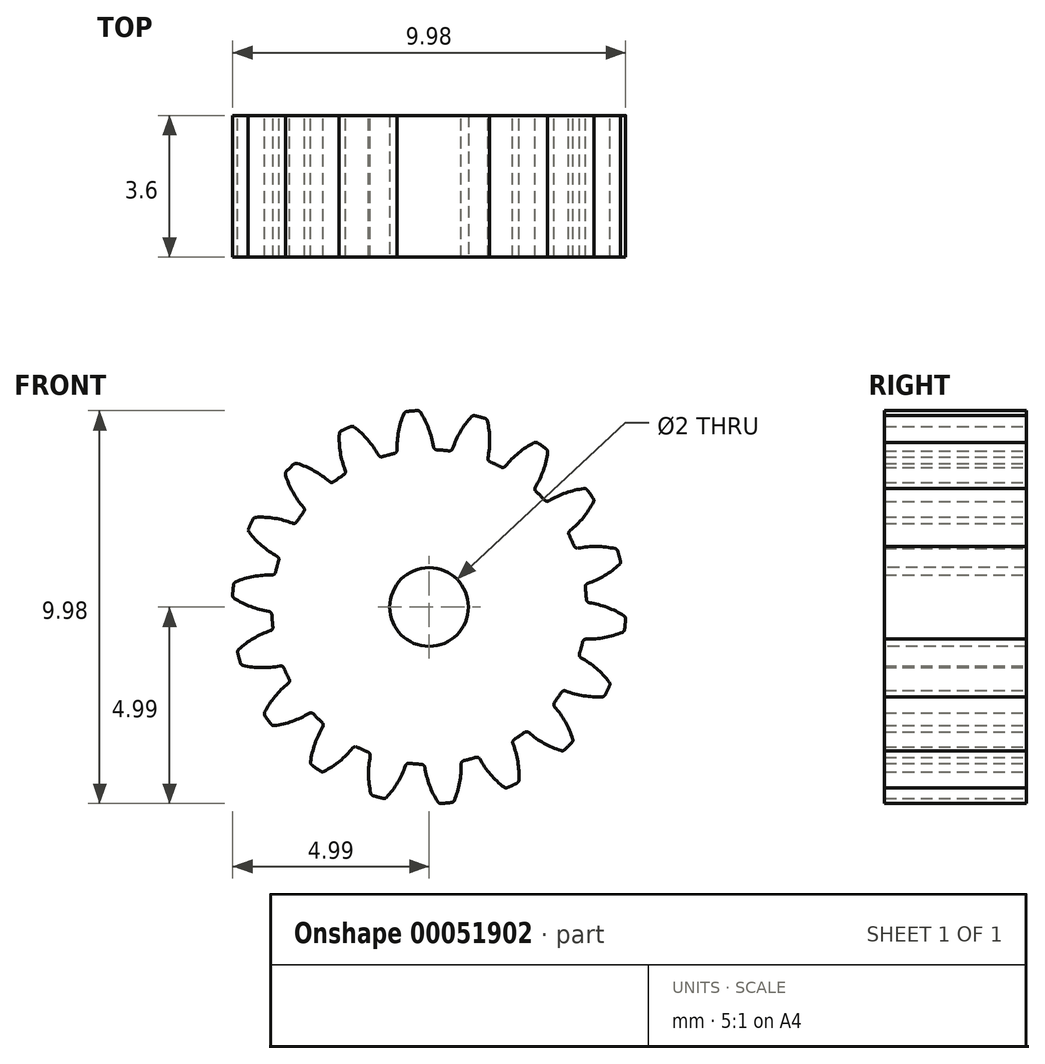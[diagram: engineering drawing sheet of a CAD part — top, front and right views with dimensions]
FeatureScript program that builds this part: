
annotation { "Feature Type Name" : "Feature", "Feature Type Description" : "" }
export const myFeature = defineFeature(function(context is Context, id is Id, definition is map)
    precondition{}
    {
        {
            var Q0;
            Q0=qCreatedBy(makeId("Front.planeOp"),FACE);
            var sketch = newSketch(context, id + "F0", { "sketchPlane" : qUnion([Q0])});
            skCircle(sketch, "E0", {"center": v(0, 0) * mm, "radius": 5 * mm, "construction": true});
            skCircle(sketch, "E1", {"center": v(0, 0) * mm, "radius": 4.5 * mm, "construction": true});
            skCircle(sketch, "E2", {"center": v(0, 0) * mm, "radius": 4 * mm, "construction": true});
            skLineSegment(sketch, "E3", {"start": v(0, 0) * mm, "end": v(0, 8.94) * mm, "construction": true});
            skLineSegment(sketch, "E4", {"start": v(0, 0) * mm, "end": v(-0.76, 8.67) * mm, "construction": true});
            skLineSegment(sketch, "E5", {"start": v(0, 4.5) * mm, "end": v(-8.84, 4.5) * mm, "construction": true});
            skLineSegment(sketch, "E6", {"start": v(0, 4.5) * mm, "end": v(-8.62, 1.36) * mm, "construction": true});
            skCircle(sketch, "E7", {"center": v(0, 4.5) * mm, "radius": 2.25 * mm, "construction": true});
            skCircle(sketch, "E8", {"center": v(-2.11, 3.73) * mm, "radius": 2.25 * mm, "construction": true});
            skArc(sketch, "E9", {"start": v(-0.25, 5) * mm, "mid": v(0, 4.52) * mm, "end": v(0.12, 4) * mm, "construction": true});
            skArc(sketch, "E10", {"start": v(-0.22, 4.95) * mm, "mid": v(-0.01, 4.53) * mm, "end": v(0.1, 4.07) * mm});
            skArc(sketch, "E11.MirrorCS", {"start": v(-0.64, 4.91) * mm, "mid": v(-0.78, 4.46) * mm, "end": v(-0.82, 4) * mm});
            skArc(sketch, "E12", {"start": v(-0.57, 4.97) * mm, "mid": v(-0.44, 4.98) * mm, "end": v(-0.3, 5) * mm});
            skArc(sketch, "E13", {"start": v(-0.89, 3.9) * mm, "mid": v(0.35, -3.98) * mm, "end": v(0.2, 4) * mm});
            skPoint(sketch, "E14.visualSharp", {"position": v(-0.81, 3.92) * mm});
            skArc(sketch, "E14.filletArc", {"start": v(-0.89, 3.9) * mm, "mid": v(-0.83, 3.93) * mm, "end": v(-0.82, 4) * mm});
            skPoint(sketch, "E15.visualSharp", {"position": v(-0.62, 4.96) * mm});
            skArc(sketch, "E15.filletArc", {"start": v(-0.57, 4.97) * mm, "mid": v(-0.61, 4.95) * mm, "end": v(-0.64, 4.91) * mm});
            skPoint(sketch, "E16.visualSharp", {"position": v(0.12, 4) * mm});
            skArc(sketch, "E16.filletArc", {"start": v(0.1, 4.07) * mm, "mid": v(0.14, 4.02) * mm, "end": v(0.2, 4) * mm});
            skPoint(sketch, "E17.visualSharp", {"position": v(-0.25, 5) * mm});
            skArc(sketch, "E17.filletArc", {"start": v(-0.22, 4.95) * mm, "mid": v(-0.26, 4.98) * mm, "end": v(-0.3, 5) * mm});
            skArc(sketch, "E18.1.0", {"start": v(-2.17, 3.36) * mm, "mid": v(-2.13, 3.41) * mm, "end": v(-2.13, 3.47) * mm});
            skArc(sketch, "E18.1.1", {"start": v(-2.28, 4.4) * mm, "mid": v(-2.26, 3.93) * mm, "end": v(-2.13, 3.47) * mm});
            skArc(sketch, "E18.1.2", {"start": v(-2.23, 4.47) * mm, "mid": v(-2.27, 4.44) * mm, "end": v(-2.28, 4.4) * mm});
            skArc(sketch, "E18.1.3", {"start": v(-2.23, 4.47) * mm, "mid": v(-2.11, 4.53) * mm, "end": v(-2, 4.59) * mm});
            skArc(sketch, "E18.1.4", {"start": v(-1.9, 4.57) * mm, "mid": v(-1.95, 4.6) * mm, "end": v(-2, 4.59) * mm});
            skArc(sketch, "E18.1.5", {"start": v(-1.9, 4.57) * mm, "mid": v(-1.56, 4.25) * mm, "end": v(-1.29, 3.86) * mm});
            skArc(sketch, "E18.1.6", {"start": v(-1.29, 3.86) * mm, "mid": v(-1.24, 3.82) * mm, "end": v(-1.18, 3.82) * mm});
            skArc(sketch, "E18.2.0", {"start": v(-3.19, 2.42) * mm, "mid": v(-3.17, 2.48) * mm, "end": v(-3.19, 2.53) * mm});
            skArc(sketch, "E18.2.1", {"start": v(-3.65, 3.35) * mm, "mid": v(-3.46, 2.92) * mm, "end": v(-3.19, 2.53) * mm});
            skArc(sketch, "E18.2.2", {"start": v(-3.63, 3.44) * mm, "mid": v(-3.65, 3.4) * mm, "end": v(-3.65, 3.35) * mm});
            skArc(sketch, "E18.2.3", {"start": v(-3.63, 3.44) * mm, "mid": v(-3.54, 3.54) * mm, "end": v(-3.44, 3.63) * mm});
            skArc(sketch, "E18.2.4", {"start": v(-3.35, 3.65) * mm, "mid": v(-3.4, 3.65) * mm, "end": v(-3.44, 3.63) * mm});
            skArc(sketch, "E18.2.5", {"start": v(-3.35, 3.65) * mm, "mid": v(-2.92, 3.46) * mm, "end": v(-2.53, 3.19) * mm});
            skArc(sketch, "E18.2.6", {"start": v(-2.53, 3.19) * mm, "mid": v(-2.48, 3.17) * mm, "end": v(-2.42, 3.19) * mm});
            skArc(sketch, "E18.3.0", {"start": v(-3.82, 1.18) * mm, "mid": v(-3.82, 1.24) * mm, "end": v(-3.86, 1.29) * mm});
            skArc(sketch, "E18.3.1", {"start": v(-4.57, 1.9) * mm, "mid": v(-4.25, 1.56) * mm, "end": v(-3.86, 1.29) * mm});
            skArc(sketch, "E18.3.2", {"start": v(-4.59, 2) * mm, "mid": v(-4.6, 1.95) * mm, "end": v(-4.57, 1.9) * mm});
            skArc(sketch, "E18.3.3", {"start": v(-4.59, 2) * mm, "mid": v(-4.53, 2.11) * mm, "end": v(-4.47, 2.23) * mm});
            skArc(sketch, "E18.3.4", {"start": v(-4.4, 2.28) * mm, "mid": v(-4.44, 2.27) * mm, "end": v(-4.47, 2.23) * mm});
            skArc(sketch, "E18.3.5", {"start": v(-4.4, 2.28) * mm, "mid": v(-3.93, 2.26) * mm, "end": v(-3.47, 2.13) * mm});
            skArc(sketch, "E18.3.6", {"start": v(-3.47, 2.13) * mm, "mid": v(-3.41, 2.13) * mm, "end": v(-3.36, 2.17) * mm});
            skArc(sketch, "E18.4.0", {"start": v(-4, -0.2) * mm, "mid": v(-4.02, -0.14) * mm, "end": v(-4.07, -0.1) * mm});
            skArc(sketch, "E18.4.1", {"start": v(-4.95, 0.22) * mm, "mid": v(-4.53, 0.01) * mm, "end": v(-4.07, -0.1) * mm});
            skArc(sketch, "E18.4.2", {"start": v(-5, 0.3) * mm, "mid": v(-4.98, 0.26) * mm, "end": v(-4.95, 0.22) * mm});
            skArc(sketch, "E18.4.3", {"start": v(-5, 0.3) * mm, "mid": v(-4.98, 0.44) * mm, "end": v(-4.97, 0.57) * mm});
            skArc(sketch, "E18.4.4", {"start": v(-4.91, 0.64) * mm, "mid": v(-4.95, 0.61) * mm, "end": v(-4.97, 0.57) * mm});
            skArc(sketch, "E18.4.5", {"start": v(-4.91, 0.64) * mm, "mid": v(-4.46, 0.78) * mm, "end": v(-4, 0.82) * mm});
            skArc(sketch, "E18.4.6", {"start": v(-4, 0.82) * mm, "mid": v(-3.93, 0.83) * mm, "end": v(-3.9, 0.89) * mm});
            skArc(sketch, "E18.5.0", {"start": v(-3.69, -1.55) * mm, "mid": v(-3.73, -1.5) * mm, "end": v(-3.79, -1.5) * mm});
            skArc(sketch, "E18.5.1", {"start": v(-4.73, -1.48) * mm, "mid": v(-4.26, -1.54) * mm, "end": v(-3.79, -1.5) * mm});
            skArc(sketch, "E18.5.2", {"start": v(-4.8, -1.42) * mm, "mid": v(-4.77, -1.46) * mm, "end": v(-4.73, -1.48) * mm});
            skArc(sketch, "E18.5.3", {"start": v(-4.8, -1.42) * mm, "mid": v(-4.83, -1.3) * mm, "end": v(-4.86, -1.17) * mm});
            skArc(sketch, "E18.5.4", {"start": v(-4.84, -1.08) * mm, "mid": v(-4.86, -1.12) * mm, "end": v(-4.86, -1.17) * mm});
            skArc(sketch, "E18.5.5", {"start": v(-4.84, -1.08) * mm, "mid": v(-4.46, -0.8) * mm, "end": v(-4.03, -0.6) * mm});
            skArc(sketch, "E18.5.6", {"start": v(-4.03, -0.6) * mm, "mid": v(-3.98, -0.56) * mm, "end": v(-3.97, -0.5) * mm});
            skArc(sketch, "E18.6.0", {"start": v(-2.94, -2.72) * mm, "mid": v(-2.99, -2.69) * mm, "end": v(-3.05, -2.7) * mm});
            skArc(sketch, "E18.6.1", {"start": v(-3.94, -3.01) * mm, "mid": v(-3.48, -2.9) * mm, "end": v(-3.05, -2.7) * mm});
            skArc(sketch, "E18.6.2", {"start": v(-4.02, -2.97) * mm, "mid": v(-3.98, -3) * mm, "end": v(-3.94, -3.01) * mm});
            skArc(sketch, "E18.6.3", {"start": v(-4.02, -2.97) * mm, "mid": v(-4.1, -2.87) * mm, "end": v(-4.17, -2.76) * mm});
            skArc(sketch, "E18.6.4", {"start": v(-4.17, -2.67) * mm, "mid": v(-4.18, -2.71) * mm, "end": v(-4.17, -2.76) * mm});
            skArc(sketch, "E18.6.5", {"start": v(-4.17, -2.67) * mm, "mid": v(-3.92, -2.27) * mm, "end": v(-3.58, -1.94) * mm});
            skArc(sketch, "E18.6.6", {"start": v(-3.58, -1.94) * mm, "mid": v(-3.55, -1.89) * mm, "end": v(-3.56, -1.83) * mm});
            skArc(sketch, "E18.7.0", {"start": v(-1.83, -3.56) * mm, "mid": v(-1.89, -3.55) * mm, "end": v(-1.94, -3.58) * mm});
            skArc(sketch, "E18.7.1", {"start": v(-2.67, -4.17) * mm, "mid": v(-2.27, -3.92) * mm, "end": v(-1.94, -3.58) * mm});
            skArc(sketch, "E18.7.2", {"start": v(-2.76, -4.17) * mm, "mid": v(-2.71, -4.18) * mm, "end": v(-2.67, -4.17) * mm});
            skArc(sketch, "E18.7.3", {"start": v(-2.76, -4.17) * mm, "mid": v(-2.87, -4.1) * mm, "end": v(-2.97, -4.02) * mm});
            skArc(sketch, "E18.7.4", {"start": v(-3.01, -3.94) * mm, "mid": v(-3, -3.98) * mm, "end": v(-2.97, -4.02) * mm});
            skArc(sketch, "E18.7.5", {"start": v(-3.01, -3.94) * mm, "mid": v(-2.9, -3.48) * mm, "end": v(-2.7, -3.05) * mm});
            skArc(sketch, "E18.7.6", {"start": v(-2.7, -3.05) * mm, "mid": v(-2.69, -2.99) * mm, "end": v(-2.72, -2.94) * mm});
            skArc(sketch, "E18.8.0", {"start": v(-0.5, -3.97) * mm, "mid": v(-0.56, -3.98) * mm, "end": v(-0.6, -4.03) * mm});
            skArc(sketch, "E18.8.1", {"start": v(-1.08, -4.84) * mm, "mid": v(-0.8, -4.46) * mm, "end": v(-0.6, -4.03) * mm});
            skArc(sketch, "E18.8.2", {"start": v(-1.17, -4.86) * mm, "mid": v(-1.12, -4.86) * mm, "end": v(-1.08, -4.84) * mm});
            skArc(sketch, "E18.8.3", {"start": v(-1.17, -4.86) * mm, "mid": v(-1.3, -4.83) * mm, "end": v(-1.42, -4.8) * mm});
            skArc(sketch, "E18.8.4", {"start": v(-1.48, -4.73) * mm, "mid": v(-1.46, -4.77) * mm, "end": v(-1.42, -4.8) * mm});
            skArc(sketch, "E18.8.5", {"start": v(-1.48, -4.73) * mm, "mid": v(-1.54, -4.26) * mm, "end": v(-1.5, -3.79) * mm});
            skArc(sketch, "E18.8.6", {"start": v(-1.5, -3.79) * mm, "mid": v(-1.5, -3.73) * mm, "end": v(-1.55, -3.69) * mm});
            skArc(sketch, "E18.9.0", {"start": v(0.89, -3.9) * mm, "mid": v(0.83, -3.93) * mm, "end": v(0.82, -4) * mm});
            skArc(sketch, "E18.9.1", {"start": v(0.64, -4.91) * mm, "mid": v(0.78, -4.46) * mm, "end": v(0.82, -4) * mm});
            skArc(sketch, "E18.9.2", {"start": v(0.57, -4.97) * mm, "mid": v(0.61, -4.95) * mm, "end": v(0.64, -4.91) * mm});
            skArc(sketch, "E18.9.3", {"start": v(0.57, -4.97) * mm, "mid": v(0.44, -4.98) * mm, "end": v(0.3, -5) * mm});
            skArc(sketch, "E18.9.4", {"start": v(0.22, -4.95) * mm, "mid": v(0.26, -4.98) * mm, "end": v(0.3, -5) * mm});
            skArc(sketch, "E18.9.5", {"start": v(0.22, -4.95) * mm, "mid": v(0.01, -4.53) * mm, "end": v(-0.1, -4.07) * mm});
            skArc(sketch, "E18.9.6", {"start": v(-0.1, -4.07) * mm, "mid": v(-0.14, -4.02) * mm, "end": v(-0.2, -4) * mm});
            skArc(sketch, "E18.10.0", {"start": v(2.17, -3.36) * mm, "mid": v(2.13, -3.41) * mm, "end": v(2.13, -3.47) * mm});
            skArc(sketch, "E18.10.1", {"start": v(2.28, -4.4) * mm, "mid": v(2.26, -3.93) * mm, "end": v(2.13, -3.47) * mm});
            skArc(sketch, "E18.10.2", {"start": v(2.23, -4.47) * mm, "mid": v(2.27, -4.44) * mm, "end": v(2.28, -4.4) * mm});
            skArc(sketch, "E18.10.3", {"start": v(2.23, -4.47) * mm, "mid": v(2.11, -4.53) * mm, "end": v(2, -4.59) * mm});
            skArc(sketch, "E18.10.4", {"start": v(1.9, -4.57) * mm, "mid": v(1.95, -4.6) * mm, "end": v(2, -4.59) * mm});
            skArc(sketch, "E18.10.5", {"start": v(1.9, -4.57) * mm, "mid": v(1.56, -4.25) * mm, "end": v(1.29, -3.86) * mm});
            skArc(sketch, "E18.10.6", {"start": v(1.29, -3.86) * mm, "mid": v(1.24, -3.82) * mm, "end": v(1.18, -3.82) * mm});
            skArc(sketch, "E18.11.0", {"start": v(3.19, -2.42) * mm, "mid": v(3.17, -2.48) * mm, "end": v(3.19, -2.53) * mm});
            skArc(sketch, "E18.11.1", {"start": v(3.65, -3.35) * mm, "mid": v(3.46, -2.92) * mm, "end": v(3.19, -2.53) * mm});
            skArc(sketch, "E18.11.2", {"start": v(3.63, -3.44) * mm, "mid": v(3.65, -3.4) * mm, "end": v(3.65, -3.35) * mm});
            skArc(sketch, "E18.11.3", {"start": v(3.63, -3.44) * mm, "mid": v(3.54, -3.54) * mm, "end": v(3.44, -3.63) * mm});
            skArc(sketch, "E18.11.4", {"start": v(3.35, -3.65) * mm, "mid": v(3.4, -3.65) * mm, "end": v(3.44, -3.63) * mm});
            skArc(sketch, "E18.11.5", {"start": v(3.35, -3.65) * mm, "mid": v(2.92, -3.46) * mm, "end": v(2.53, -3.19) * mm});
            skArc(sketch, "E18.11.6", {"start": v(2.53, -3.19) * mm, "mid": v(2.48, -3.17) * mm, "end": v(2.42, -3.19) * mm});
            skArc(sketch, "E18.12.0", {"start": v(3.82, -1.18) * mm, "mid": v(3.82, -1.24) * mm, "end": v(3.86, -1.29) * mm});
            skArc(sketch, "E18.12.1", {"start": v(4.57, -1.9) * mm, "mid": v(4.25, -1.56) * mm, "end": v(3.86, -1.29) * mm});
            skArc(sketch, "E18.12.2", {"start": v(4.59, -2) * mm, "mid": v(4.6, -1.95) * mm, "end": v(4.57, -1.9) * mm});
            skArc(sketch, "E18.12.3", {"start": v(4.59, -2) * mm, "mid": v(4.53, -2.11) * mm, "end": v(4.47, -2.23) * mm});
            skArc(sketch, "E18.12.4", {"start": v(4.4, -2.28) * mm, "mid": v(4.44, -2.27) * mm, "end": v(4.47, -2.23) * mm});
            skArc(sketch, "E18.12.5", {"start": v(4.4, -2.28) * mm, "mid": v(3.93, -2.26) * mm, "end": v(3.47, -2.13) * mm});
            skArc(sketch, "E18.12.6", {"start": v(3.47, -2.13) * mm, "mid": v(3.41, -2.13) * mm, "end": v(3.36, -2.17) * mm});
            skArc(sketch, "E18.13.0", {"start": v(4, 0.2) * mm, "mid": v(4.02, 0.14) * mm, "end": v(4.07, 0.1) * mm});
            skArc(sketch, "E18.13.1", {"start": v(4.95, -0.22) * mm, "mid": v(4.53, -0.01) * mm, "end": v(4.07, 0.1) * mm});
            skArc(sketch, "E18.13.2", {"start": v(5, -0.3) * mm, "mid": v(4.98, -0.26) * mm, "end": v(4.95, -0.22) * mm});
            skArc(sketch, "E18.13.3", {"start": v(5, -0.3) * mm, "mid": v(4.98, -0.44) * mm, "end": v(4.97, -0.57) * mm});
            skArc(sketch, "E18.13.4", {"start": v(4.91, -0.64) * mm, "mid": v(4.95, -0.61) * mm, "end": v(4.97, -0.57) * mm});
            skArc(sketch, "E18.13.5", {"start": v(4.91, -0.64) * mm, "mid": v(4.46, -0.78) * mm, "end": v(4, -0.82) * mm});
            skArc(sketch, "E18.13.6", {"start": v(4, -0.82) * mm, "mid": v(3.93, -0.83) * mm, "end": v(3.9, -0.89) * mm});
            skArc(sketch, "E18.14.0", {"start": v(3.69, 1.55) * mm, "mid": v(3.73, 1.5) * mm, "end": v(3.79, 1.5) * mm});
            skArc(sketch, "E18.14.1", {"start": v(4.73, 1.48) * mm, "mid": v(4.26, 1.54) * mm, "end": v(3.79, 1.5) * mm});
            skArc(sketch, "E18.14.2", {"start": v(4.8, 1.42) * mm, "mid": v(4.77, 1.46) * mm, "end": v(4.73, 1.48) * mm});
            skArc(sketch, "E18.14.3", {"start": v(4.8, 1.42) * mm, "mid": v(4.83, 1.3) * mm, "end": v(4.86, 1.17) * mm});
            skArc(sketch, "E18.14.4", {"start": v(4.84, 1.08) * mm, "mid": v(4.86, 1.12) * mm, "end": v(4.86, 1.17) * mm});
            skArc(sketch, "E18.14.5", {"start": v(4.84, 1.08) * mm, "mid": v(4.46, 0.8) * mm, "end": v(4.03, 0.6) * mm});
            skArc(sketch, "E18.14.6", {"start": v(4.03, 0.6) * mm, "mid": v(3.98, 0.56) * mm, "end": v(3.97, 0.5) * mm});
            skArc(sketch, "E18.15.0", {"start": v(2.94, 2.72) * mm, "mid": v(2.99, 2.69) * mm, "end": v(3.05, 2.7) * mm});
            skArc(sketch, "E18.15.1", {"start": v(3.94, 3.01) * mm, "mid": v(3.48, 2.9) * mm, "end": v(3.05, 2.7) * mm});
            skArc(sketch, "E18.15.2", {"start": v(4.02, 2.97) * mm, "mid": v(3.98, 3) * mm, "end": v(3.94, 3.01) * mm});
            skArc(sketch, "E18.15.3", {"start": v(4.02, 2.97) * mm, "mid": v(4.1, 2.87) * mm, "end": v(4.17, 2.76) * mm});
            skArc(sketch, "E18.15.4", {"start": v(4.17, 2.67) * mm, "mid": v(4.18, 2.71) * mm, "end": v(4.17, 2.76) * mm});
            skArc(sketch, "E18.15.5", {"start": v(4.17, 2.67) * mm, "mid": v(3.92, 2.27) * mm, "end": v(3.58, 1.94) * mm});
            skArc(sketch, "E18.15.6", {"start": v(3.58, 1.94) * mm, "mid": v(3.55, 1.89) * mm, "end": v(3.56, 1.83) * mm});
            skArc(sketch, "E18.16.0", {"start": v(1.83, 3.56) * mm, "mid": v(1.89, 3.55) * mm, "end": v(1.94, 3.58) * mm});
            skArc(sketch, "E18.16.1", {"start": v(2.67, 4.17) * mm, "mid": v(2.27, 3.92) * mm, "end": v(1.94, 3.58) * mm});
            skArc(sketch, "E18.16.2", {"start": v(2.76, 4.17) * mm, "mid": v(2.71, 4.18) * mm, "end": v(2.67, 4.17) * mm});
            skArc(sketch, "E18.16.3", {"start": v(2.76, 4.17) * mm, "mid": v(2.87, 4.1) * mm, "end": v(2.97, 4.02) * mm});
            skArc(sketch, "E18.16.4", {"start": v(3.01, 3.94) * mm, "mid": v(3, 3.98) * mm, "end": v(2.97, 4.02) * mm});
            skArc(sketch, "E18.16.5", {"start": v(3.01, 3.94) * mm, "mid": v(2.9, 3.48) * mm, "end": v(2.7, 3.05) * mm});
            skArc(sketch, "E18.16.6", {"start": v(2.7, 3.05) * mm, "mid": v(2.69, 2.99) * mm, "end": v(2.72, 2.94) * mm});
            skArc(sketch, "E18.17.0", {"start": v(0.5, 3.97) * mm, "mid": v(0.56, 3.98) * mm, "end": v(0.6, 4.03) * mm});
            skArc(sketch, "E18.17.1", {"start": v(1.08, 4.84) * mm, "mid": v(0.8, 4.46) * mm, "end": v(0.6, 4.03) * mm});
            skArc(sketch, "E18.17.2", {"start": v(1.17, 4.86) * mm, "mid": v(1.12, 4.86) * mm, "end": v(1.08, 4.84) * mm});
            skArc(sketch, "E18.17.3", {"start": v(1.17, 4.86) * mm, "mid": v(1.3, 4.83) * mm, "end": v(1.42, 4.8) * mm});
            skArc(sketch, "E18.17.4", {"start": v(1.48, 4.73) * mm, "mid": v(1.46, 4.77) * mm, "end": v(1.42, 4.8) * mm});
            skArc(sketch, "E18.17.5", {"start": v(1.48, 4.73) * mm, "mid": v(1.54, 4.26) * mm, "end": v(1.5, 3.79) * mm});
            skArc(sketch, "E18.17.6", {"start": v(1.5, 3.79) * mm, "mid": v(1.5, 3.73) * mm, "end": v(1.55, 3.69) * mm});
            skSolve(sketch);
        }
        {
            var Q0;
            Q0=qSketchRegion(id+"F0",true);
            var Q1;
            Q1=makeQuery(id+"F0.imprint","IMPRINT",FACE,{"disambiguationData":[TD([[makeQuery(id+"F0.imprint","IMPRINT",EDGE,{"derivedFrom":sQuery(id+"F0.wireOp",EDGE,"E10")}),-1.0]])]});
            extrude(context, id + "F1", {"entities" : qUnion([Q0, Q1]), "depth" : 3.6 * mm});
        }
        {
            var Q0;
            Q0=makeQuery(id+"F1.opExtrude","CAP_FACE",FACE,{"disambiguationData":[OSD([sQuery(id+"F0.wireOp",EDGE,"E10"),sQuery(id+"F0.wireOp",EDGE,"E11.MirrorCS"),sQuery(id+"F0.wireOp",EDGE,"E12"),sQuery(id+"F0.wireOp",EDGE,"E13"),sQuery(id+"F0.wireOp",EDGE,"E14.filletArc"),sQuery(id+"F0.wireOp",EDGE,"E15.filletArc"),sQuery(id+"F0.wireOp",EDGE,"E16.filletArc"),sQuery(id+"F0.wireOp",EDGE,"E17.filletArc"),sQuery(id+"F0.wireOp",EDGE,"E18.1.0"),sQuery(id+"F0.wireOp",EDGE,"E18.1.1"),sQuery(id+"F0.wireOp",EDGE,"E18.1.2"),sQuery(id+"F0.wireOp",EDGE,"E18.1.3"),sQuery(id+"F0.wireOp",EDGE,"E18.1.4"),sQuery(id+"F0.wireOp",EDGE,"E18.1.5"),sQuery(id+"F0.wireOp",EDGE,"E18.1.6"),sQuery(id+"F0.wireOp",EDGE,"E18.2.0"),sQuery(id+"F0.wireOp",EDGE,"E18.2.1"),sQuery(id+"F0.wireOp",EDGE,"E18.2.2"),sQuery(id+"F0.wireOp",EDGE,"E18.2.3"),sQuery(id+"F0.wireOp",EDGE,"E18.2.4"),sQuery(id+"F0.wireOp",EDGE,"E18.2.5"),sQuery(id+"F0.wireOp",EDGE,"E18.2.6"),sQuery(id+"F0.wireOp",EDGE,"E18.3.0"),sQuery(id+"F0.wireOp",EDGE,"E18.3.1"),sQuery(id+"F0.wireOp",EDGE,"E18.3.2"),sQuery(id+"F0.wireOp",EDGE,"E18.3.3"),sQuery(id+"F0.wireOp",EDGE,"E18.3.4"),sQuery(id+"F0.wireOp",EDGE,"E18.3.5"),sQuery(id+"F0.wireOp",EDGE,"E18.3.6"),sQuery(id+"F0.wireOp",EDGE,"E18.4.0"),sQuery(id+"F0.wireOp",EDGE,"E18.4.1"),sQuery(id+"F0.wireOp",EDGE,"E18.4.2"),sQuery(id+"F0.wireOp",EDGE,"E18.4.3"),sQuery(id+"F0.wireOp",EDGE,"E18.4.4"),sQuery(id+"F0.wireOp",EDGE,"E18.4.5"),sQuery(id+"F0.wireOp",EDGE,"E18.4.6"),sQuery(id+"F0.wireOp",EDGE,"E18.5.0"),sQuery(id+"F0.wireOp",EDGE,"E18.5.1"),sQuery(id+"F0.wireOp",EDGE,"E18.5.2"),sQuery(id+"F0.wireOp",EDGE,"E18.5.3"),sQuery(id+"F0.wireOp",EDGE,"E18.5.4"),sQuery(id+"F0.wireOp",EDGE,"E18.5.5"),sQuery(id+"F0.wireOp",EDGE,"E18.5.6"),sQuery(id+"F0.wireOp",EDGE,"E18.6.0"),sQuery(id+"F0.wireOp",EDGE,"E18.6.1"),sQuery(id+"F0.wireOp",EDGE,"E18.6.2"),sQuery(id+"F0.wireOp",EDGE,"E18.6.3"),sQuery(id+"F0.wireOp",EDGE,"E18.6.4"),sQuery(id+"F0.wireOp",EDGE,"E18.6.5"),sQuery(id+"F0.wireOp",EDGE,"E18.6.6"),sQuery(id+"F0.wireOp",EDGE,"E18.7.0"),sQuery(id+"F0.wireOp",EDGE,"E18.7.1"),sQuery(id+"F0.wireOp",EDGE,"E18.7.2"),sQuery(id+"F0.wireOp",EDGE,"E18.7.3"),sQuery(id+"F0.wireOp",EDGE,"E18.7.4"),sQuery(id+"F0.wireOp",EDGE,"E18.7.5"),sQuery(id+"F0.wireOp",EDGE,"E18.7.6"),sQuery(id+"F0.wireOp",EDGE,"E18.8.0"),sQuery(id+"F0.wireOp",EDGE,"E18.8.1"),sQuery(id+"F0.wireOp",EDGE,"E18.8.2"),sQuery(id+"F0.wireOp",EDGE,"E18.8.3"),sQuery(id+"F0.wireOp",EDGE,"E18.8.4"),sQuery(id+"F0.wireOp",EDGE,"E18.8.5"),sQuery(id+"F0.wireOp",EDGE,"E18.8.6"),sQuery(id+"F0.wireOp",EDGE,"E18.9.0"),sQuery(id+"F0.wireOp",EDGE,"E18.9.1"),sQuery(id+"F0.wireOp",EDGE,"E18.9.2"),sQuery(id+"F0.wireOp",EDGE,"E18.9.3"),sQuery(id+"F0.wireOp",EDGE,"E18.9.4"),sQuery(id+"F0.wireOp",EDGE,"E18.9.5"),sQuery(id+"F0.wireOp",EDGE,"E18.9.6"),sQuery(id+"F0.wireOp",EDGE,"E18.10.0"),sQuery(id+"F0.wireOp",EDGE,"E18.10.1"),sQuery(id+"F0.wireOp",EDGE,"E18.10.2"),sQuery(id+"F0.wireOp",EDGE,"E18.10.3"),sQuery(id+"F0.wireOp",EDGE,"E18.10.4"),sQuery(id+"F0.wireOp",EDGE,"E18.10.5"),sQuery(id+"F0.wireOp",EDGE,"E18.10.6"),sQuery(id+"F0.wireOp",EDGE,"E18.11.0"),sQuery(id+"F0.wireOp",EDGE,"E18.11.1"),sQuery(id+"F0.wireOp",EDGE,"E18.11.2"),sQuery(id+"F0.wireOp",EDGE,"E18.11.3"),sQuery(id+"F0.wireOp",EDGE,"E18.11.4"),sQuery(id+"F0.wireOp",EDGE,"E18.11.5"),sQuery(id+"F0.wireOp",EDGE,"E18.11.6"),sQuery(id+"F0.wireOp",EDGE,"E18.12.0"),sQuery(id+"F0.wireOp",EDGE,"E18.12.1"),sQuery(id+"F0.wireOp",EDGE,"E18.12.2"),sQuery(id+"F0.wireOp",EDGE,"E18.12.3"),sQuery(id+"F0.wireOp",EDGE,"E18.12.4"),sQuery(id+"F0.wireOp",EDGE,"E18.12.5"),sQuery(id+"F0.wireOp",EDGE,"E18.12.6"),sQuery(id+"F0.wireOp",EDGE,"E18.13.0"),sQuery(id+"F0.wireOp",EDGE,"E18.13.1"),sQuery(id+"F0.wireOp",EDGE,"E18.13.2"),sQuery(id+"F0.wireOp",EDGE,"E18.13.3"),sQuery(id+"F0.wireOp",EDGE,"E18.13.4"),sQuery(id+"F0.wireOp",EDGE,"E18.13.5"),sQuery(id+"F0.wireOp",EDGE,"E18.13.6"),sQuery(id+"F0.wireOp",EDGE,"E18.14.0"),sQuery(id+"F0.wireOp",EDGE,"E18.14.1"),sQuery(id+"F0.wireOp",EDGE,"E18.14.2"),sQuery(id+"F0.wireOp",EDGE,"E18.14.3"),sQuery(id+"F0.wireOp",EDGE,"E18.14.4"),sQuery(id+"F0.wireOp",EDGE,"E18.14.5"),sQuery(id+"F0.wireOp",EDGE,"E18.14.6"),sQuery(id+"F0.wireOp",EDGE,"E18.15.0"),sQuery(id+"F0.wireOp",EDGE,"E18.15.1"),sQuery(id+"F0.wireOp",EDGE,"E18.15.2"),sQuery(id+"F0.wireOp",EDGE,"E18.15.3"),sQuery(id+"F0.wireOp",EDGE,"E18.15.4"),sQuery(id+"F0.wireOp",EDGE,"E18.15.5"),sQuery(id+"F0.wireOp",EDGE,"E18.15.6"),sQuery(id+"F0.wireOp",EDGE,"E18.16.0"),sQuery(id+"F0.wireOp",EDGE,"E18.16.1"),sQuery(id+"F0.wireOp",EDGE,"E18.16.2"),sQuery(id+"F0.wireOp",EDGE,"E18.16.3"),sQuery(id+"F0.wireOp",EDGE,"E18.16.4"),sQuery(id+"F0.wireOp",EDGE,"E18.16.5"),sQuery(id+"F0.wireOp",EDGE,"E18.16.6"),sQuery(id+"F0.wireOp",EDGE,"E18.17.0"),sQuery(id+"F0.wireOp",EDGE,"E18.17.1"),sQuery(id+"F0.wireOp",EDGE,"E18.17.2"),sQuery(id+"F0.wireOp",EDGE,"E18.17.3"),sQuery(id+"F0.wireOp",EDGE,"E18.17.4"),sQuery(id+"F0.wireOp",EDGE,"E18.17.5"),sQuery(id+"F0.wireOp",EDGE,"E18.17.6")])],"isStart":false});
            var sketch = newSketch(context, id + "F2", { "sketchPlane" : qUnion([Q0])});
            skCircle(sketch, "E19", {"center": v(0, 0) * mm, "radius": 1 * mm});
            skSolve(sketch);
        }
        {
            var Q0;
            Q0=qSketchRegion(id+"F2",true);
            extrude(context, id + "F3", {"entities" : qUnion([Q0]), "operationType" : NewBodyOperationType.REMOVE, "endBound" : BoundingType.THROUGH_ALL, "oppositeDirection" : true, "depth" : 25 * mm});
        }
    });
